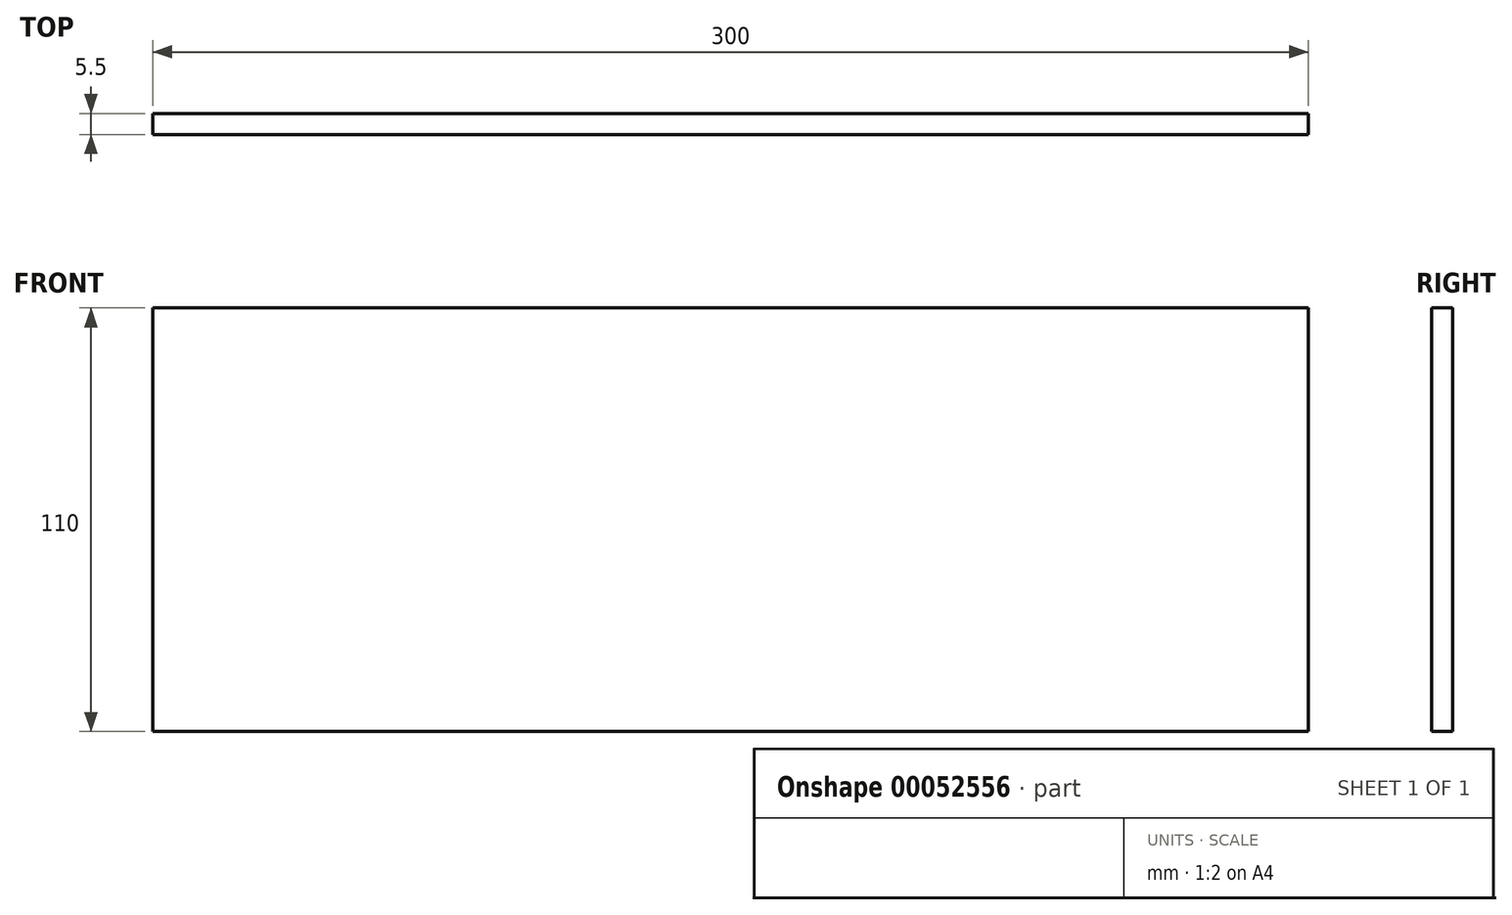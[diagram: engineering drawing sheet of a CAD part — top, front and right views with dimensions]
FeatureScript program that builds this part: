
annotation { "Feature Type Name" : "Feature", "Feature Type Description" : "" }
export const myFeature = defineFeature(function(context is Context, id is Id, definition is map)
    precondition{}
    {
        {
            var Q0;
            Q0=qCreatedBy(makeId("Front.planeOp"),FACE);
            var sketch = newSketch(context, id + "F0", { "sketchPlane" : qUnion([Q0])});
            skLineSegment(sketch, "E0.bottom", {"start": v(0, 0) * mm, "end": v(-300, 0) * mm});
            skLineSegment(sketch, "E0.top", {"start": v(0, 110) * mm, "end": v(-300, 110) * mm});
            skLineSegment(sketch, "E0.left", {"start": v(0, 0) * mm, "end": v(0, 110) * mm});
            skLineSegment(sketch, "E0.right", {"start": v(-300, 0) * mm, "end": v(-300, 110) * mm});
            skSolve(sketch);
        }
        {
            var Q0;
            Q0 = qSketchRegion(id + "F0", true);
            extrude(context, id + "F1", {"entities" : qUnion([Q0]), "oppositeDirection" : true, "depth" : 5.5 * mm});
        }
    });
